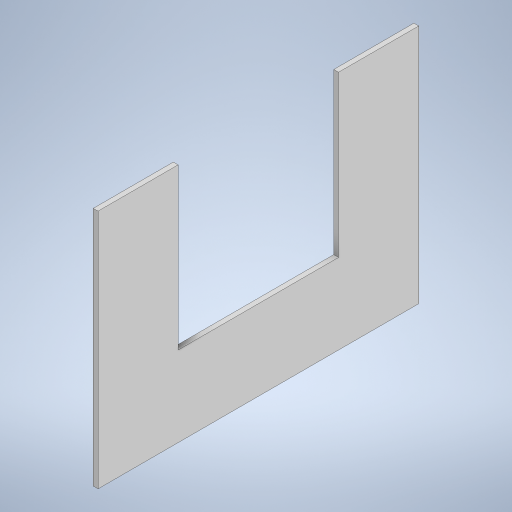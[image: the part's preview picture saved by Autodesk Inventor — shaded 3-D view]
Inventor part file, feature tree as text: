
AUTODESK INVENTOR PART (.ipt)
format: ipt  version: 2024.3 (Build 283343000, 343)  size: 213,504 bytes
history: native  units: mm
features: extrude x1, sketch x1
ambient origin geometry x8: Origin, YZ Plane, XZ Plane, XY Plane, X Axis, Y Axis, Z Axis, Center Point
bodies: Solid1 (feature_tree)
feature tree (2):
  extrude  "Extrusion1"  Depth=150.0mm
  sketch  "Sketch1"  dims[d0=200.0mm d1=150.0mm d2=100.0mm d3=100.0mm d4=50.0mm d5=3.0mm d6=0.0mm]
